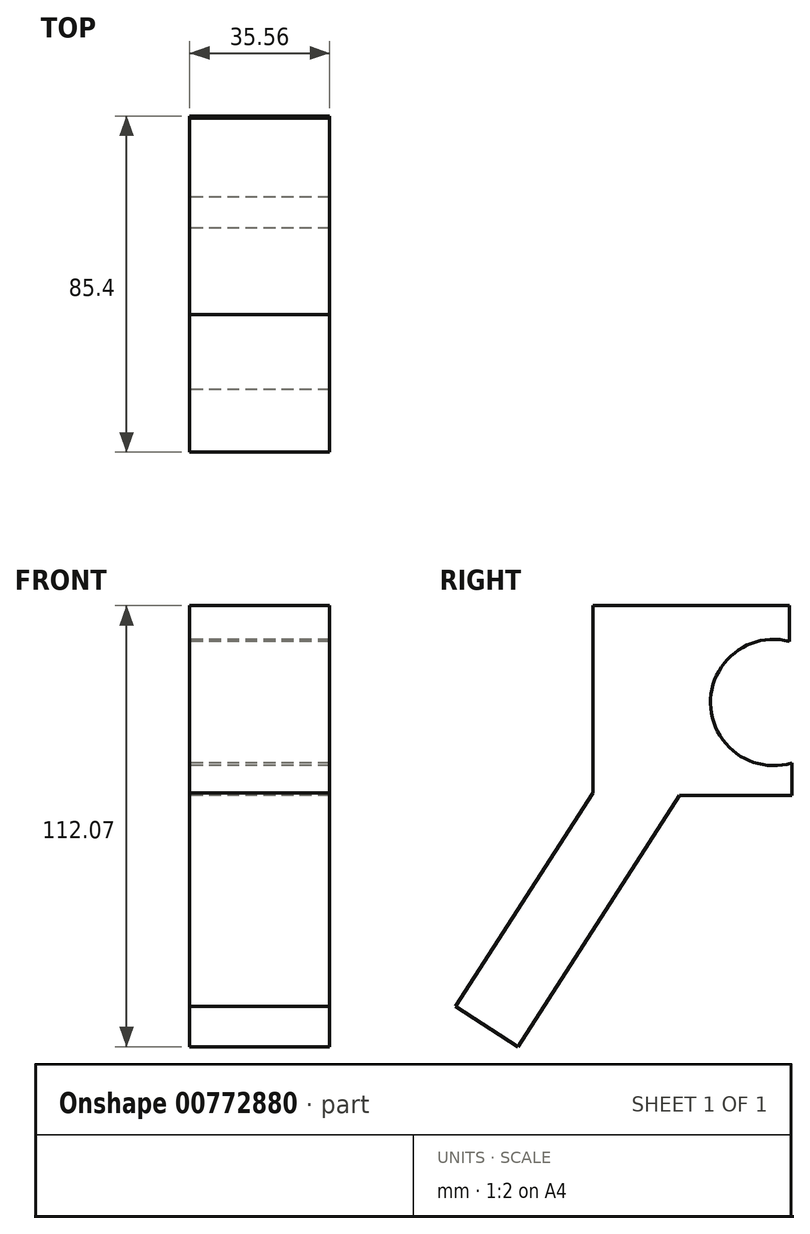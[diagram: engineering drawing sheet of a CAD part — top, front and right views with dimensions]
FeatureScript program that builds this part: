
annotation { "Feature Type Name" : "Feature", "Feature Type Description" : "" }
export const myFeature = defineFeature(function(context is Context, id is Id, definition is map)
    precondition{}
    {
        {
            var Q0;
            Q0=qCreatedBy(makeId("Right.planeOp"),FACE);
            var sketch = newSketch(context, id + "F0", { "sketchPlane" : qUnion([Q0])});
            skLineSegment(sketch, "E0", {"start": v(-51.5, -44.69) * mm, "end": v(-67.38, -34.47) * mm});
            skLineSegment(sketch, "E1", {"start": v(-67.38, -34.47) * mm, "end": v(-45.22, 0) * mm});
            skLineSegment(sketch, "E2", {"start": v(-51.5, -44.69) * mm, "end": v(-26.8, -6.28) * mm});
            skLineSegment(sketch, "E3", {"start": v(-45.22, 0) * mm, "end": v(-32.5, 19.8) * mm});
            skLineSegment(sketch, "E4", {"start": v(-32.5, 19.8) * mm, "end": v(-32.5, 67.38) * mm});
            skLineSegment(sketch, "E5", {"start": v(-32.5, 67.38) * mm, "end": v(17.45, 67.38) * mm});
            skLineSegment(sketch, "E6", {"start": v(-26.8, -6.28) * mm, "end": v(-10.5, 19.08) * mm});
            skLineSegment(sketch, "E7", {"start": v(-10.5, 19.08) * mm, "end": v(18.02, 19.08) * mm});
            skLineSegment(sketch, "E8", {"start": v(18.02, 19.08) * mm, "end": v(18.02, 27.38) * mm});
            skLineSegment(sketch, "E9", {"start": v(17.45, 67.38) * mm, "end": v(17.45, 58.3) * mm});
            skArc(sketch, "E10", {"start": v(17.45, 58.3) * mm, "mid": v(-2.6, 42.47) * mm, "end": v(18.02, 27.38) * mm});
            skSolve(sketch);
        }
        {
            var Q0;
            Q0=makeQuery(id+"F0.imprint","IMPRINT",FACE,{"disambiguationData":[TD([[makeQuery(id+"F0.imprint","IMPRINT",EDGE,{"derivedFrom":sQuery(id+"F0.wireOp",EDGE,"E0")}),-1.0]])]});
            extrude(context, id + "F1", {"entities" : qUnion([Q0]), "endBound" : BoundingType.SYMMETRIC, "depth" : 35.56 * mm, "offsetDistance" : 25.4 * mm});
        }
    });
